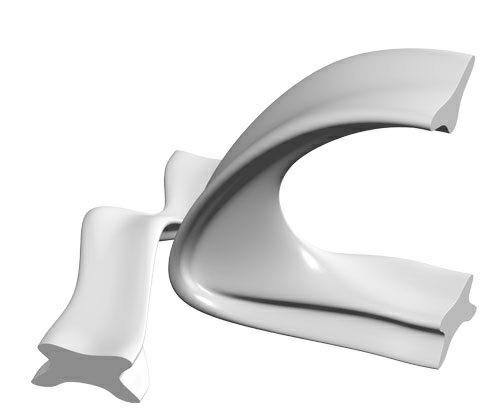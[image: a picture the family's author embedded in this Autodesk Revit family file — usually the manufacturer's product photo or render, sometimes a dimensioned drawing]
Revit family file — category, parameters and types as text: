
# Revit family: CITY ALPHABET letter „K”
name_source: partatom
category: Furniture
revit_build: Autodesk Revit 2018 (Build: 20190510_1515(x64)
units: mm (PartAtom-declared; Revit-internal decimal feet)

## family parameters
Cut with Voids When Loaded = No
Host = Face
OmniClass Number = 23.40.10.11.14
OmniClass Title = Exterior Seating
Room Calculation Point = No
Shared = No

## types (1)
- CITY ALPHABET letter „K”
    Default Elevation = 1219 mm
    Height = 1900 mm  [stored 6.2336 ft]
    IfcExportAs = IfcFurnishingElement
    Length = 2400 mm
    Manufacturer = Astrini Design
    Material information = Colour choice from RAL colour standard. Customer may inquire about specific request regarding individual order.
    Model = CITY ALPHABET letter „K”
    Operating temperature = -40°C to 80°C, ( -40°F to 176°F )
    Type Comments = Bench
    Type Image = K.jpg
    URL = https://astrini-design.pl
    Weight (approximately) = 115.00 kg
    Weight - filled (approximately) = 215.00 kg
    Width = 2400 mm

note: [stored X ft] marks values corroborated as IEEE doubles in the binary element streams (Revit-internal decimal feet)
